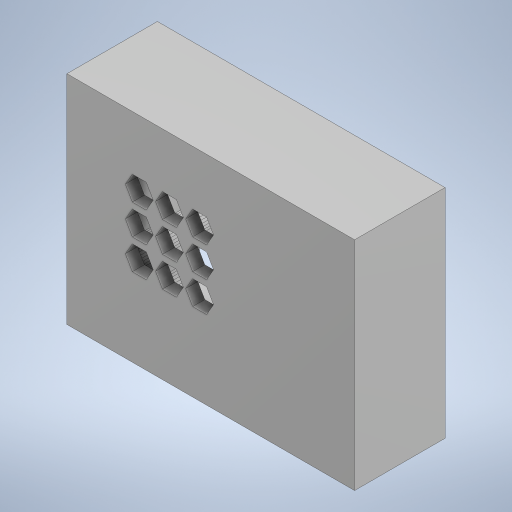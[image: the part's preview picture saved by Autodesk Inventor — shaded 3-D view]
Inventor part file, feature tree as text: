
AUTODESK INVENTOR PART (.ipt)
format: ipt  version: 2024.3 (Build 283343000, 343)  size: 542,208 bytes
history: native  units: mm
features: other x3, extrude x1, sketch x1
ambient origin geometry x8: Origin, YZ Plane, XZ Plane, XY Plane, X Axis, Y Axis, Z Axis, Center Point
bodies: Body1 (feature_tree)
feature tree (5):
  other  "Sólido1"
  other  "LP8-BASE v1"
  other  "MeshFeature1"
  extrude  "Extrusión1"  Depth=16.0mm
  sketch  "Boceto1"  dims[d0=10.0mm d1=16.0mm d2=6.0mm d3=3.0mm d4=0.0mm]
